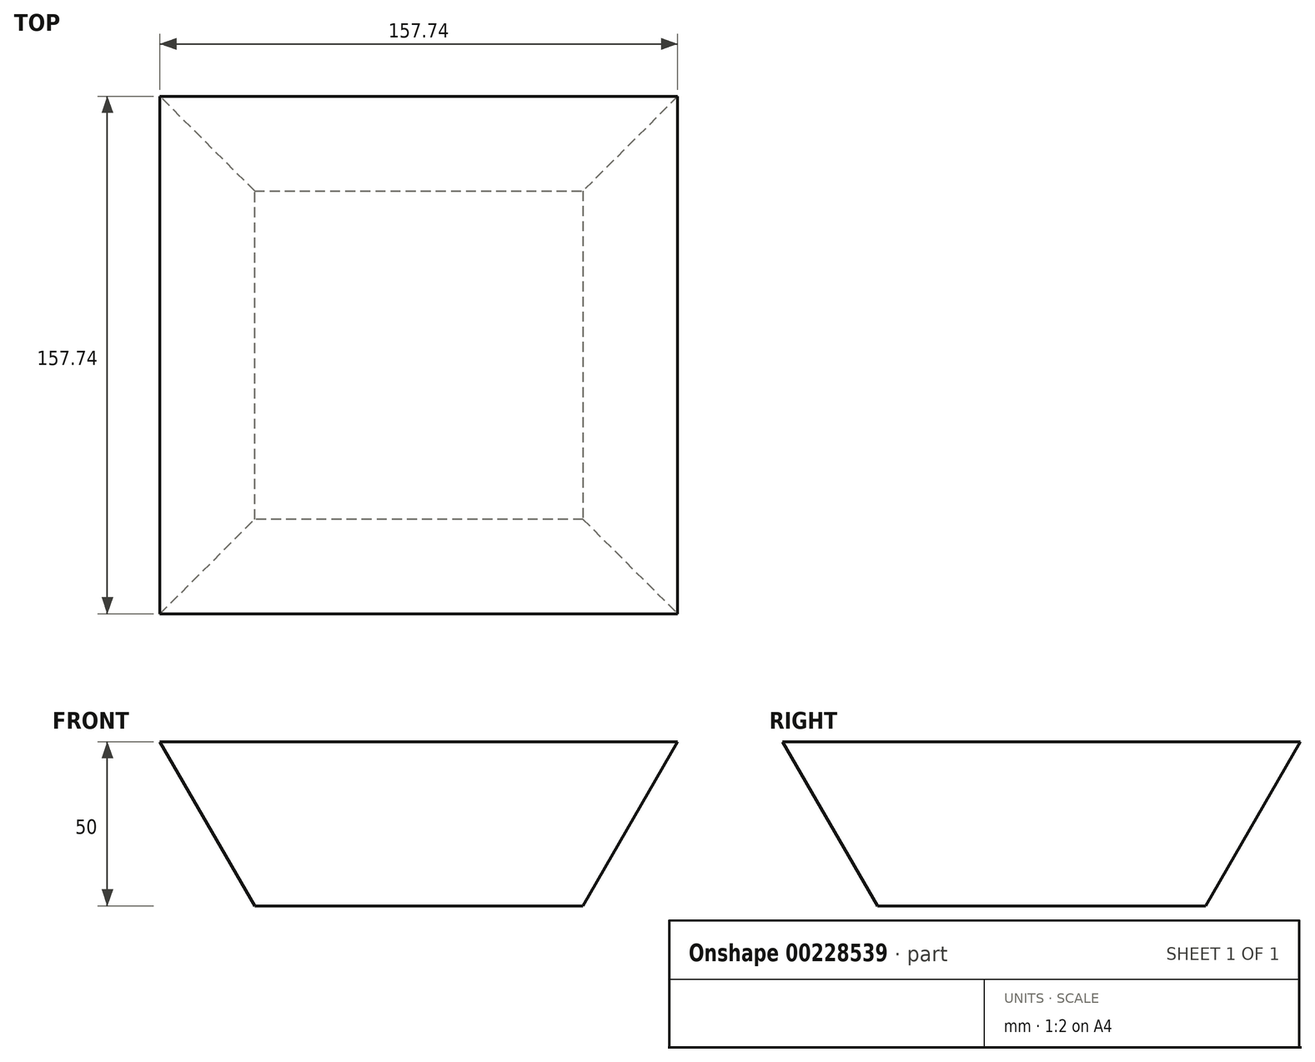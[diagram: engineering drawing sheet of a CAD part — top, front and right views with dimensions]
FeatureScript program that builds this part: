
annotation { "Feature Type Name" : "Feature", "Feature Type Description" : "" }
export const myFeature = defineFeature(function(context is Context, id is Id, definition is map)
    precondition{}
    {
        {
            var Q0;
            Q0=qCreatedBy(makeId("Top.planeOp"),FACE);
            var sketch = newSketch(context, id + "F0", { "sketchPlane" : qUnion([Q0])});
            skLineSegment(sketch, "E0.bottom", {"start": v(50, -50) * mm, "end": v(-50, -50) * mm});
            skLineSegment(sketch, "E0.top", {"start": v(50, 50) * mm, "end": v(-50, 50) * mm});
            skLineSegment(sketch, "E0.left", {"start": v(50, -50) * mm, "end": v(50, 50) * mm});
            skLineSegment(sketch, "E0.right", {"start": v(-50, -50) * mm, "end": v(-50, 50) * mm});
            skPoint(sketch, "E0.middle", {"position": v(0, 0) * mm});
            skSolve(sketch);
        }
        {
            var Q0;
            Q0 = qSketchRegion(id + "F0", true);
            extrude(context, id + "F1", {"entities" : qUnion([Q0]), "depth" : 50 * mm, "hasDraft" : true, "draftAngle" : 30 * degree});
        }
    });
